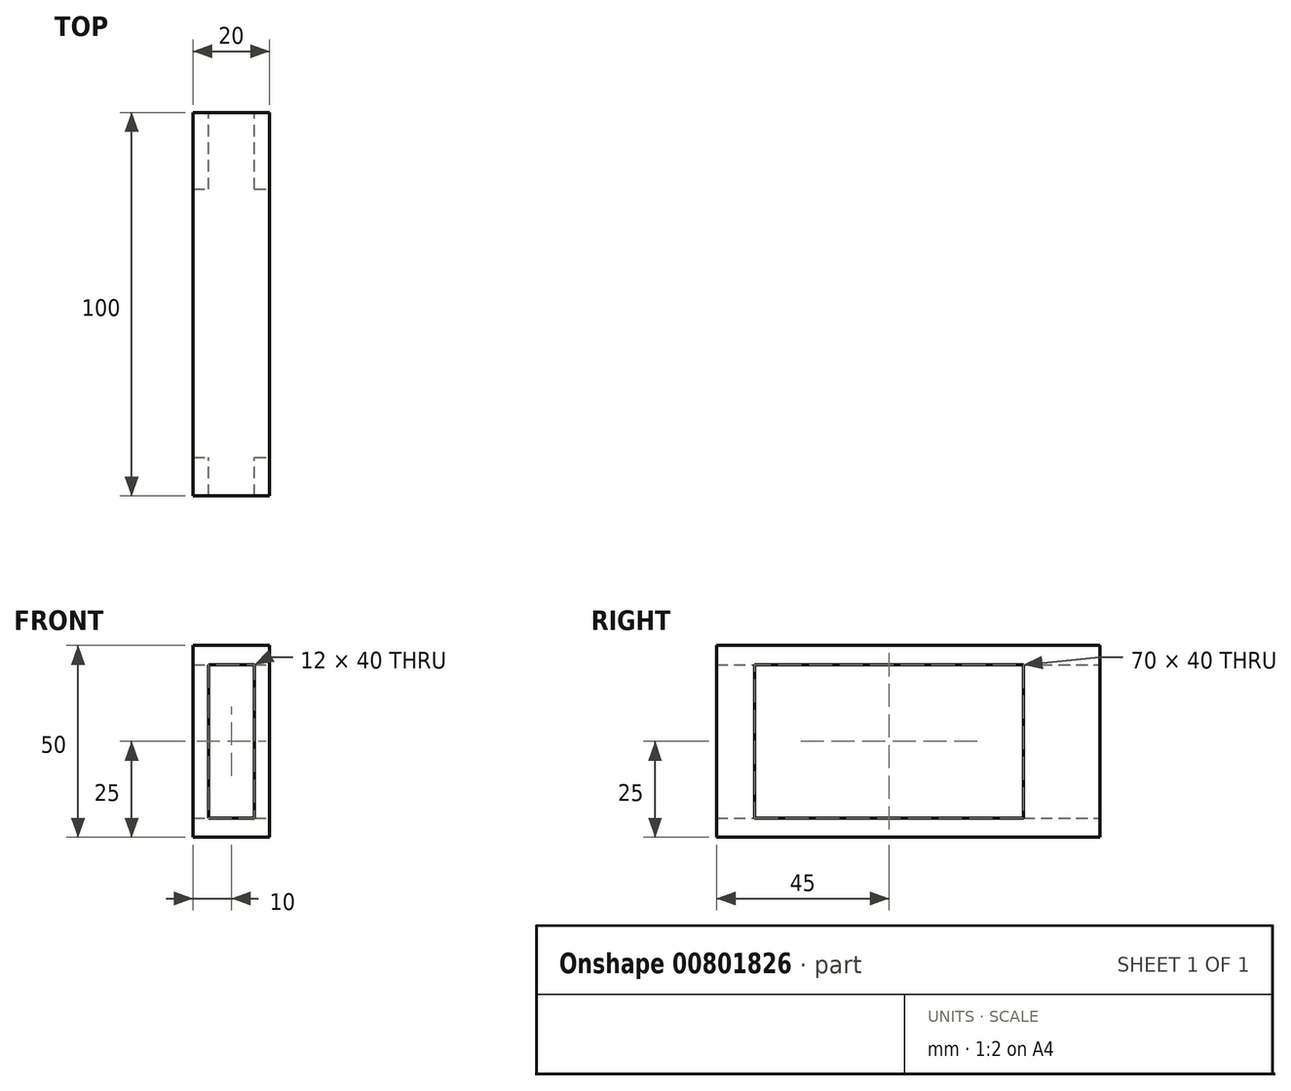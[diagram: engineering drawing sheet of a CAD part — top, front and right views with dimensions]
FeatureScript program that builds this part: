
annotation { "Feature Type Name" : "Feature", "Feature Type Description" : "" }
export const myFeature = defineFeature(function(context is Context, id is Id, definition is map)
    precondition{}
    {
        {
            var Q0;
            Q0=qCreatedBy(makeId("Front.planeOp"),FACE);
            var sketch = newSketch(context, id + "F0", { "sketchPlane" : qUnion([Q0])});
            skLineSegment(sketch, "E0.bottom", {"start": v(0, 0) * mm, "end": v(20, 0) * mm});
            skLineSegment(sketch, "E0.top", {"start": v(0, -50) * mm, "end": v(20, -50) * mm});
            skLineSegment(sketch, "E0.left", {"start": v(0, 0) * mm, "end": v(0, -50) * mm});
            skLineSegment(sketch, "E0.right", {"start": v(20, 0) * mm, "end": v(20, -50) * mm});
            skLineSegment(sketch, "E1.bottom", {"start": v(4, -5) * mm, "end": v(16, -5) * mm});
            skLineSegment(sketch, "E1.top", {"start": v(4, -45) * mm, "end": v(16, -45) * mm});
            skLineSegment(sketch, "E1.left", {"start": v(4, -5) * mm, "end": v(4, -45) * mm});
            skLineSegment(sketch, "E1.right", {"start": v(16, -5) * mm, "end": v(16, -45) * mm});
            skSolve(sketch);
        }
        {
            var Q0;
            Q0=makeQuery(id+"F0.imprint","IMPRINT",FACE,{"disambiguationData":[TD([[makeQuery(id+"F0.imprint","IMPRINT",EDGE,{"derivedFrom":sQuery(id+"F0.wireOp",EDGE,"E0.bottom")}),-1.0]])]});
            extrude(context, id + "F1", {"entities" : qUnion([Q0]), "depth" : 100 * mm, "offsetDistance" : 25 * mm});
        }
        {
            var Q0;
            Q0=makeQuery(id+"F1.opExtrude","SWEPT_FACE",FACE,{"disambiguationData":[OSD([sQuery(id+"F0.wireOp",EDGE,"E0.right")])]});
            var sketch = newSketch(context, id + "F2", { "sketchPlane" : qUnion([Q0])});
            skLineSegment(sketch, "E2.bottom", {"start": v(-90, -5) * mm, "end": v(-20, -5) * mm});
            skLineSegment(sketch, "E2.top", {"start": v(-90, -45) * mm, "end": v(-20, -45) * mm});
            skLineSegment(sketch, "E2.left", {"start": v(-90, -5) * mm, "end": v(-90, -45) * mm});
            skLineSegment(sketch, "E2.right", {"start": v(-20, -5) * mm, "end": v(-20, -45) * mm});
            skSolve(sketch);
        }
        {
            var Q0;
            Q0=makeQuery(id+"F2.imprint","IMPRINT",FACE,{"disambiguationData":[TD([[makeQuery(id+"F2.imprint","IMPRINT",EDGE,{"derivedFrom":sQuery(id+"F2.wireOp",EDGE,"E2.bottom")}),-1.0]])]});
            extrude(context, id + "F3", {"entities" : qUnion([Q0]), "operationType" : NewBodyOperationType.REMOVE, "oppositeDirection" : true, "depth" : 25 * mm, "offsetDistance" : 25 * mm});
        }
    });
